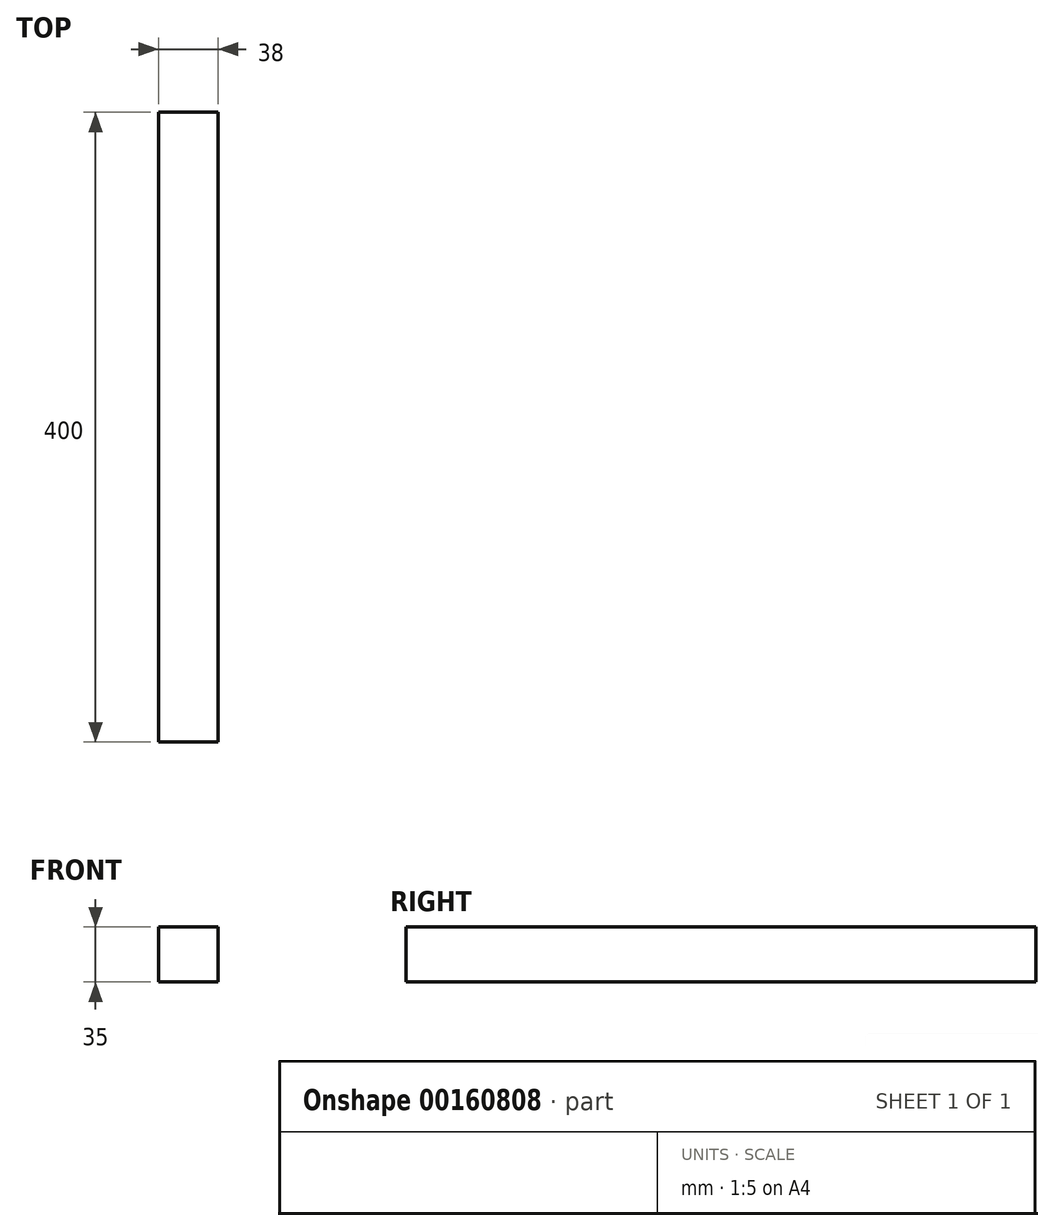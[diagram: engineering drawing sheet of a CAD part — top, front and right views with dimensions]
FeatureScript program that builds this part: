
annotation { "Feature Type Name" : "Feature", "Feature Type Description" : "" }
export const myFeature = defineFeature(function(context is Context, id is Id, definition is map)
    precondition{}
    {
        {
            var Q0;
            Q0=qCreatedBy(makeId("Front.planeOp"),FACE);
            var sketch = newSketch(context, id + "F0", { "sketchPlane" : qUnion([Q0])});
            skLineSegment(sketch, "E0.bottom", {"start": v(-109.11, 58.89) * mm, "end": v(-71.11, 58.89) * mm});
            skLineSegment(sketch, "E0.top", {"start": v(-109.11, 23.89) * mm, "end": v(-71.11, 23.89) * mm});
            skLineSegment(sketch, "E0.left", {"start": v(-109.11, 58.89) * mm, "end": v(-109.11, 23.89) * mm});
            skLineSegment(sketch, "E0.right", {"start": v(-71.11, 58.89) * mm, "end": v(-71.11, 23.89) * mm});
            skSolve(sketch);
        }
        {
            var Q0;
            Q0=makeQuery(id+"F0.imprint","IMPRINT",FACE,{"disambiguationData":[TD([[makeQuery(id+"F0.imprint","IMPRINT",EDGE,{"derivedFrom":sQuery(id+"F0.wireOp",EDGE,"E0.bottom")}),-1.0]])]});
            extrude(context, id + "F1", {"entities" : qUnion([Q0]), "depth" : 400 * mm});
        }
    });
